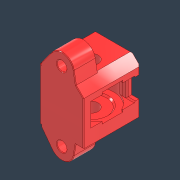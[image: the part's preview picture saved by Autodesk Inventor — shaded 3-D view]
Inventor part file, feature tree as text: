
AUTODESK INVENTOR PART (.ipt)
format: ipt  version: 2022 (Build 260153000, 153)  size: 775,168 bytes
history: native  units: mm
features: extrude x24, sketch x22, projected_geometry x21, chamfer x11, reference x11, delete_face x7, move_body x5, direct_edit x4, fillet x3, other x3, plane x2, hole x1, mirror x1
ambient origin geometry x8: Origin, YZ Plane, XZ Plane, XY Plane, X Axis, Y Axis, Z Axis, Center Point
bodies: Volumenkörper1 (feature_tree)
feature tree (115):
  extrude  "Extrusion1"  Depth=18.0mm
  extrude  "Extrusion2"  Depth=5.0mm
  plane  "Arbeitsebene1"
  extrude  "Extrusion3"  Depth=16.0mm
  extrude  "Extrusion4"  Depth=10.0mm
  extrude  "Extrusion5"  Depth=10.0mm
  hole  "Bohrung1"  [1 undecoded]
  extrude  "Extrusion6"  Depth=7.5mm
  chamfer  "Fase1"  Distance=7.5mm
  direct_edit  "Direktbearbeitung1"
  direct_edit  "Direktbearbeitung2"
  extrude  "Extrusion7"  TaperAngle=0.0deg  [1 undecoded]
  delete_face  "Fläche löschen1"
  delete_face  "Fläche löschen2"
  chamfer  "Fase8"  Distance=1.0mm Angle=45.0deg
  direct_edit  "Direktbearbeitung4"
  sketch  "Skizze11"  dims[d21=3.3mm d22=6.0mm d23=4.8mm d24=3.8mm d25=90.0deg d26=8.0mm d27=0.0mm d30=0.0mm d31=0.0mm d34=1.0mm d35=2.0mm d36=45.0deg]
  extrude  "Extrusion9"  TaperAngle=0.0deg  [1 undecoded]
  extrude  "Extrusion10"  Depth=10.0mm
  chamfer  "Fase10"  Distance=10.0mm
  extrude  "Extrusion13"  TaperAngle=0.0deg  [1 undecoded]
  extrude  "Extrusion19"  Depth=8.4mm
  extrude  "Extrusion20"  Depth=9.272952mm
  sketch  "Skizze20"  dims[d99=0.0mm d100=0.0mm d101=-0.25mm d106=8.4mm]
  extrude  "Extrusion21"  TaperAngle=0.0deg  [1 undecoded]
  extrude  "Extrusion22"  Depth=2.0mm
  extrude  "Extrusion23"  TaperAngle=90.0deg  [1 undecoded]
  extrude  "Extrusion24"  Depth=0.8mm
  extrude  "Extrusion25"  Depth=10.5mm TaperAngle=0.0deg
  chamfer  "Fase22"  Distance=3.0mm
  chamfer  "Fase23"  Distance=3.0mm
  fillet  "Rundung12"  Radius=11.0mm
  fillet  "Rundung13"  Radius=16.0mm
  extrude  "Extrusion26"  Depth=10.5mm TaperAngle=0.0deg
  chamfer  "Fase24"  Distance=9.5mm
  extrude  "Extrusion27"  Depth=7.2mm TaperAngle=0.0deg
  extrude  "Extrusion28"  Depth=18.0mm
  chamfer  "Fase25"  Distance=2.5mm
  fillet  "Rundung14"  Radius=8.0mm
  sketch  "Sketch26"  dims[d128=1.0mm d129=10.5mm d130=0.0mm d184=3.0mm d185=0.0mm d186=3.0mm d187=0.0mm d188=11.0mm d189=16.0mm]
  direct_edit  "Direct Edit5"
  extrude  "Extrusion29"  Depth=15.0mm
  extrude  "Extrusion30"  Depth=7.5mm TaperAngle=0.0deg
  chamfer  "Chamfer26"  Distance=0.4mm Angle=45.0deg
  delete_face  "Delete Face5"
  delete_face  "Delete Face6"
  chamfer  "Chamfer27"  Distance=0.5mm Angle=45.0deg
  delete_face  "Delete Face7"
  delete_face  "Delete Face8"
  delete_face  "Delete Face9"
  chamfer  "Chamfer28"  Distance=4.0mm
  chamfer  "Chamfer29"  Distance=4.0mm
  plane  "Work Plane3"
  extrude  "Extrusion31"  Depth=10.0mm
  extrude  "Extrusion32"  Depth=10.0mm
  mirror  "Mirror1"
  sketch  "Skizze1"  dims[d0=15.0mm d1=18.0mm]
  sketch  "Skizze2"  dims[d2=24.0mm d3=0.0mm d5=5.0mm]
  sketch  "Skizze3"  dims[d6=0.0mm d7=0.0mm d8=16.0mm]
  sketch  "Skizze4"  dims[d9=18.0mm d10=10.0mm]
  projected_geometry  "Projizierte Kontur1"
  projected_geometry  "Projizierte Kontur2"
  sketch  "Skizze5"  dims[d11=10.0mm d12=0.0mm d13=10.0mm]
  projected_geometry  "Projizierte Kontur3"
  projected_geometry  "Projizierte Kontur4"
  projected_geometry  "Projizierte Kontur5"
  sketch  "Skizze7"  dims[d14=1.5mm d15=0.0mm d16=0.0mm]
  reference  "Referenz1"
  reference  "Referenz2"
  reference  "Referenz3"
  reference  "Referenz4"
  reference  "Referenz5"
  reference  "Referenz6"
  reference  "Referenz7"
  reference  "Referenz8"
  reference  "Referenz9"
  reference  "Referenz10"
  reference  "Referenz11"
  sketch  "Skizze8"  dims[d17=7.0mm d18=30.0mm d19=7.5mm d20=0.0mm]
  projected_geometry  "Projizierte Kontur6"
  projected_geometry  "Projizierte Kontur7"
  projected_geometry  "Projizierte Kontur8"
  projected_geometry  "Projizierte Kontur10"
  sketch  "Skizze13"  dims[d40=0.0mm d41=0.0mm d42=-0.05mm d43=0.0mm d44=0.0mm d45=-0.05mm]
  projected_geometry  "Projizierte Kontur11"
  sketch  "Skizze18"  dims[d46=3.0mm d47=3.0mm d48=10.0mm d49=0.0mm]
  projected_geometry  "Projizierte Kontur17"
  sketch  "Skizze19"  dims[d93=0.4mm d94=2.0mm d95=45.0deg d96=0.0mm d97=0.0mm d98=-0.25mm]
  projected_geometry  "Projizierte Kontur18"
  sketch  "Skizze21"  dims[d107=9.272952mm d109=9.272952mm]
  projected_geometry  "Projizierte Kontur19"
  projected_geometry  "Projizierte Kontur20"
  sketch  "Skizze22"  dims[d110=10.0mm d111=0.0mm d112=0.0mm d113=0.0mm]
  projected_geometry  "Projizierte Kontur21"
  sketch  "Skizze23"  dims[d114=0.4mm d115=2.0mm d116=45.0deg d123=17.453293mm]
  projected_geometry  "Projizierte Kontur22"
  projected_geometry  "Projizierte Kontur23"
  sketch  "Skizze24"  dims[d124=135.0deg d125=90.0deg]
  projected_geometry  "Projizierte Kontur24"
  projected_geometry  "Projizierte Kontur25"
  sketch  "Skizze25"  dims[d126=1.6mm d127=0.8mm]
  projected_geometry  "Projizierte Kontur26"
  projected_geometry  "Projected Loop27"
  sketch  "Sketch27"  dims[d190=18.0mm d191=10.5mm d192=0.0mm d193=9.5mm d194=0.0mm]
  sketch  "Sketch28"  dims[d195=7.2mm d196=0.0mm d197=7.2mm d198=0.0mm]
  sketch  "Sketch29"  dims[d199=5.0mm d200=18.0mm]
  sketch  "Sketch30"  dims[d201=9.0mm d203=2.5mm d204=8.0mm d205=15.0mm d206=7.5mm d207=0.0mm d208=0.4mm d209=2.0mm d210=45.0deg d211=0.5mm d212=2.0mm d213=45.0deg d214=4.0mm d215=4.0mm d216=0.8mm d217=0.8mm d218=0.8mm d219=0.8mm d220=9.5mm d221=0.0mm d222=0.4mm d223=2.0mm d224=45.0deg d225=0.8mm d226=0.8mm d227=0.8mm d228=0.8mm d229=9.5mm d230=0.0mm d231=0.8mm d232=0.8mm d233=9.5mm d234=0.0mm d235=0.4mm d236=2.0mm d237=45.0deg d238=0.4mm d239=0.0mm d240=0.0mm d241=-11.0mm d242=0.5mm d243=1.0mm d244=10.0mm d245=0.0mm d246=0.5mm d247=1.0mm d248=10.0mm d249=0.0mm d250=0.4mm d251=2.0mm d252=45.0deg d253=0.4mm d254=2.0mm d255=45.0deg d256=0.2mm d257=2.0mm d258=45.0deg d259=0.2mm d260=2.0mm d261=45.0deg d262=5.15mm d263=0.0mm d264=0.0mm d265=10.0mm d266=0.0mm]
  other  "<userpath>\Desktop\Voron-2-2.4r1\Custom\Front_Idlers\Baugruppe1.iam"
  other  "Baugruppe1.iam"
  other  "Front_Idler1:1"
  move_body  "Verschieben1"
  move_body  "Verschieben2"
  move_body  "Verschieben9"
  move_body  "Verschieben10"
  move_body  "Move11"
note: 6 required parameter values undecoded (feature->parameter linkage not recoverable at this tier; creation-order binding heuristic only, values carry confidence <= 0.55)
